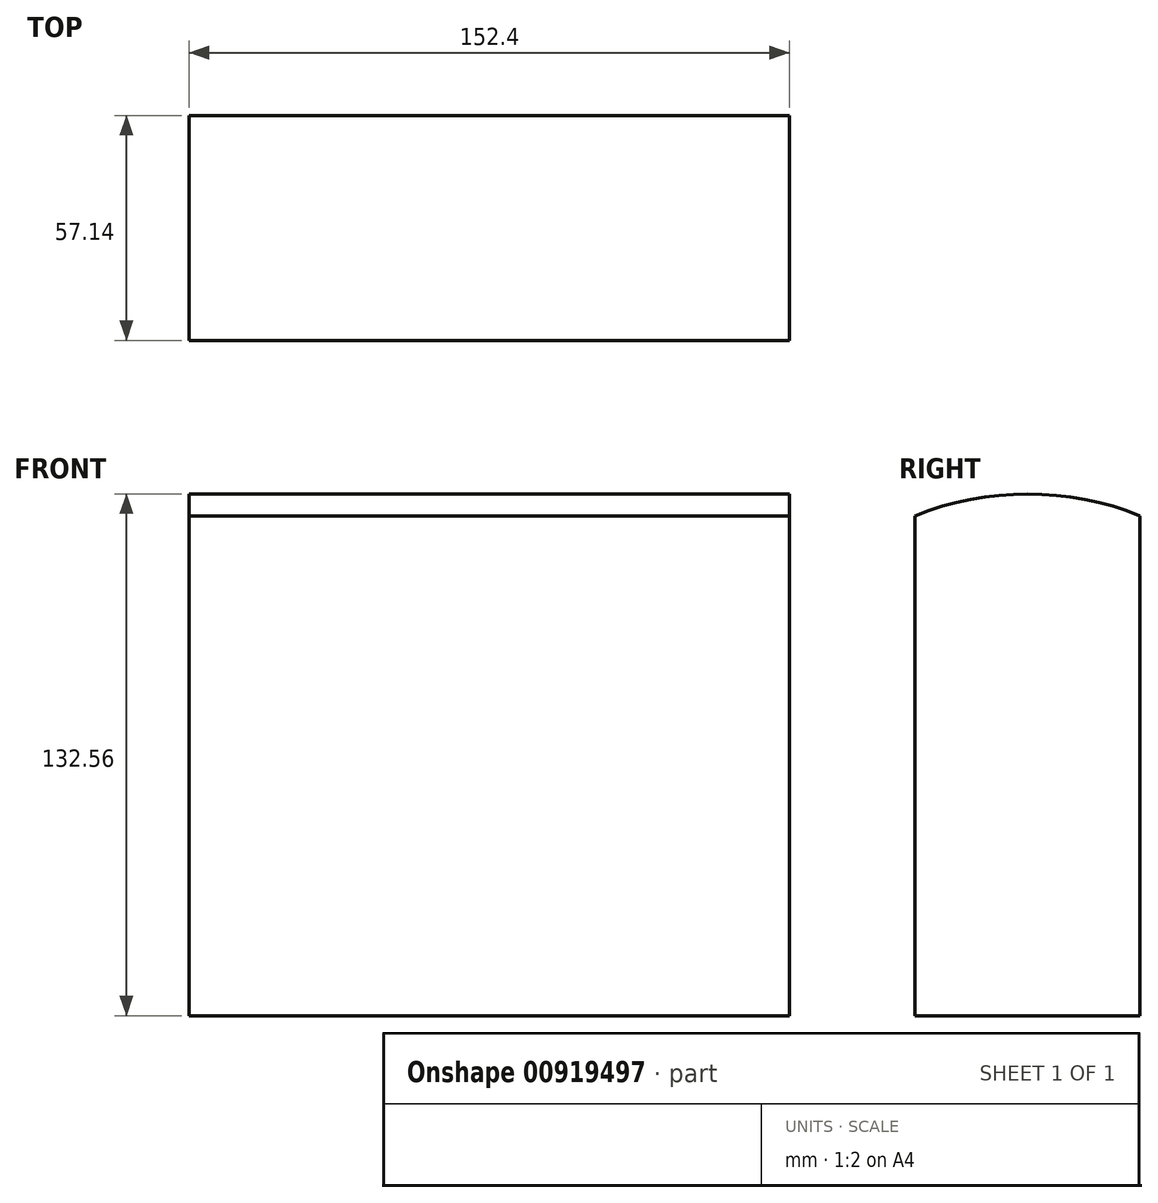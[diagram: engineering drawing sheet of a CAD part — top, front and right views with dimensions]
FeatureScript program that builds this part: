
annotation { "Feature Type Name" : "Feature", "Feature Type Description" : "" }
export const myFeature = defineFeature(function(context is Context, id is Id, definition is map)
    precondition{}
    {
        {
            var Q0;
            Q0=qCreatedBy(makeId("Right.planeOp"),FACE);
            var sketch = newSketch(context, id + "F0", { "sketchPlane" : qUnion([Q0])});
            skLineSegment(sketch, "E0.top", {"start": v(28.57, -63.5) * mm, "end": v(-28.57, -63.5) * mm});
            skLineSegment(sketch, "E0.left", {"start": v(28.58, 63.5) * mm, "end": v(28.57, -63.5) * mm});
            skLineSegment(sketch, "E0.right", {"start": v(-28.57, 63.5) * mm, "end": v(-28.58, -63.5) * mm});
            skPoint(sketch, "E0.middle", {"position": v(0, 0) * mm});
            skArc(sketch, "E1", {"start": v(-28.58, 63.5) * mm, "mid": v(0, 69.06) * mm, "end": v(28.58, 63.5) * mm});
            skSolve(sketch);
        }
        {
            var Q0;
            Q0 = qSketchRegion(id + "F0", true);
            extrude(context, id + "F1", {"entities" : qUnion([Q0]), "depth" : 76.2 * mm, "offsetDistance" : 25.4 * mm, "hasSecondDirection" : true, "secondDirectionOppositeDirection" : true, "secondDirectionDepth" : 76.2 * mm});
        }
    });
